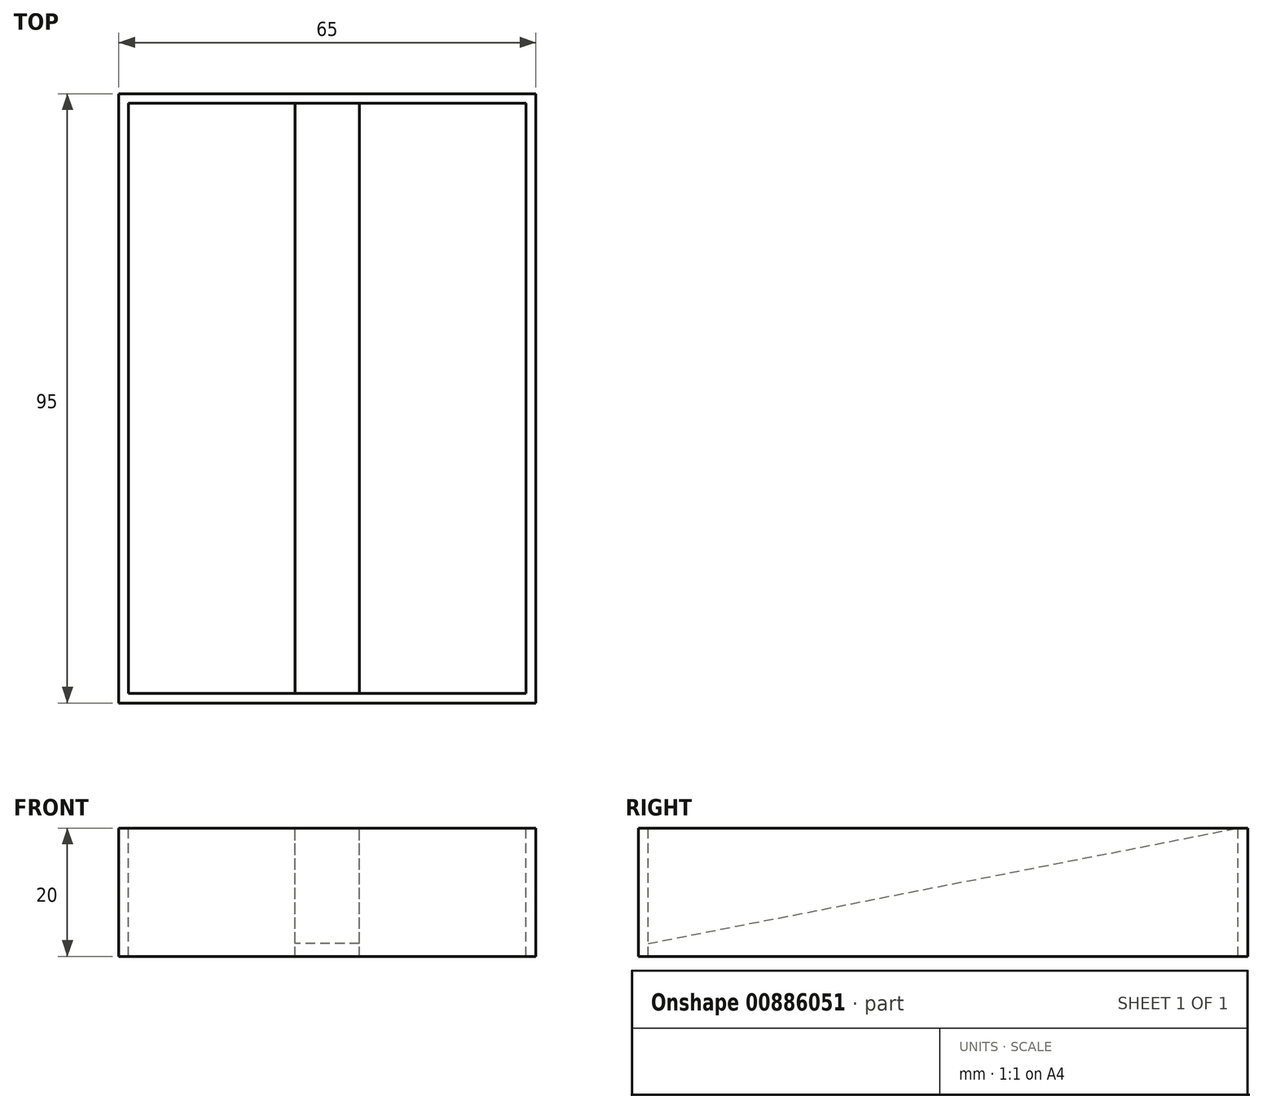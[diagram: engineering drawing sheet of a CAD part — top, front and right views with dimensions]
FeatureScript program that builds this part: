
annotation { "Feature Type Name" : "Feature", "Feature Type Description" : "" }
export const myFeature = defineFeature(function(context is Context, id is Id, definition is map)
    precondition{}
    {
        {
            var Q0;
            Q0=qCreatedBy(makeId("Top.planeOp"),FACE);
            var sketch = newSketch(context, id + "F0", { "sketchPlane" : qUnion([Q0])});
            skLineSegment(sketch, "E0.bottom", {"start": v(-32.5, -47.5) * mm, "end": v(32.5, -47.5) * mm});
            skLineSegment(sketch, "E0.top", {"start": v(-32.5, 47.5) * mm, "end": v(32.5, 47.5) * mm});
            skLineSegment(sketch, "E0.left", {"start": v(-32.5, -47.5) * mm, "end": v(-32.5, 47.5) * mm});
            skLineSegment(sketch, "E0.right", {"start": v(32.5, -47.5) * mm, "end": v(32.5, 47.5) * mm});
            skPoint(sketch, "E0.middle", {"position": v(0, 0) * mm});
            skSolve(sketch);
        }
        {
            var Q0;
            Q0=qSketchRegion(id+"F0",true);
            extrude(context, id + "F1", {"entities" : qUnion([Q0]), "depth" : 20 * mm, "offsetDistance" : 25 * mm});
        }
        {
            var Q0;
            Q0=makeQuery(id+"F1.opExtrude","CAP_FACE",FACE,{"disambiguationData":[OSD([sQuery(id+"F0.wireOp",EDGE,"E0.bottom"),sQuery(id+"F0.wireOp",EDGE,"E0.top"),sQuery(id+"F0.wireOp",EDGE,"E0.left"),sQuery(id+"F0.wireOp",EDGE,"E0.right")])],"isStart":false});
            var sketch = newSketch(context, id + "F2", { "sketchPlane" : qUnion([Q0])});
            skLineSegment(sketch, "E1.bottom", {"start": v(-31, -46) * mm, "end": v(31, -46) * mm});
            skLineSegment(sketch, "E1.top", {"start": v(-31, 46) * mm, "end": v(31, 46) * mm});
            skLineSegment(sketch, "E1.left", {"start": v(-31, -46) * mm, "end": v(-31, 46) * mm});
            skLineSegment(sketch, "E1.right", {"start": v(31, -46) * mm, "end": v(31, 46) * mm});
            skPoint(sketch, "E1.middle", {"position": v(0, 0) * mm});
            skSolve(sketch);
        }
        {
            var Q0;
            Q0=makeQuery(id+"F2.imprint","IMPRINT",FACE,{"disambiguationData":[TD([[makeQuery(id+"F2.imprint","IMPRINT",EDGE,{"derivedFrom":sQuery(id+"F2.wireOp",EDGE,"E1.bottom")}),1.0]])]});
            extrude(context, id + "F3", {"entities" : qUnion([Q0]), "operationType" : NewBodyOperationType.REMOVE, "endBound" : BoundingType.UP_TO_NEXT, "oppositeDirection" : true, "depth" : 25 * mm, "offsetDistance" : 25 * mm});
        }
        {
            var Q0;
            Q0=makeQuery(id+"F3.boolean.opBoolean","COPY",FACE,{"derivedFrom":makeQuery(id+"F3.opExtrude","SWEPT_FACE",FACE,{"disambiguationData":[OSD([sQuery(id+"F2.wireOp",EDGE,"E1.top")])]})});
            var sketch = newSketch(context, id + "F4", { "sketchPlane" : qUnion([Q0])});
            skLineSegment(sketch, "E2.bottom", {"start": v(-5, 0) * mm, "end": v(5, 0) * mm});
            skLineSegment(sketch, "E2.top", {"start": v(-5, 20) * mm, "end": v(5, 20) * mm});
            skLineSegment(sketch, "E2.left", {"start": v(-5, 0) * mm, "end": v(-5, 20) * mm});
            skLineSegment(sketch, "E2.right", {"start": v(5, 0) * mm, "end": v(5, 20) * mm});
            skSolve(sketch);
        }
        {
            var Q0;
            Q0=makeQuery(id+"F3.boolean.opBoolean","COPY",FACE,{"derivedFrom":makeQuery(id+"F3.opExtrude","SWEPT_FACE",FACE,{"disambiguationData":[OSD([sQuery(id+"F2.wireOp",EDGE,"E1.bottom")])]})});
            var sketch = newSketch(context, id + "F5", { "sketchPlane" : qUnion([Q0])});
            skLineSegment(sketch, "E3.bottom", {"start": v(-5, 0) * mm, "end": v(5, 0) * mm});
            skLineSegment(sketch, "E3.top", {"start": v(-5, 2) * mm, "end": v(5, 2) * mm});
            skLineSegment(sketch, "E3.left", {"start": v(-5, 0) * mm, "end": v(-5, 2) * mm});
            skLineSegment(sketch, "E3.right", {"start": v(5, 0) * mm, "end": v(5, 2) * mm});
            skSolve(sketch);
        }
        {
            var Q1;
            Q1=makeQuery(id+"F5.imprint","IMPRINT",FACE,{"disambiguationData":[TD([[makeQuery(id+"F5.imprint","IMPRINT",EDGE,{"derivedFrom":sQuery(id+"F5.wireOp",EDGE,"E3.bottom")}),1.0]])]});
            var Q2;
            Q2=makeQuery(id+"F4.imprint","IMPRINT",FACE,{"disambiguationData":[TD([[makeQuery(id+"F4.imprint","IMPRINT",EDGE,{"derivedFrom":sQuery(id+"F4.wireOp",EDGE,"E2.bottom")}),-1.0]])]});
            loft(context, id + "F6", {"operationType" : NewBodyOperationType.ADD, "sheetProfilesArray" : [{ "sheetProfileEntities" : qUnion([Q1]) }, { "sheetProfileEntities" : qUnion([Q2]) }]});
        }
    });
